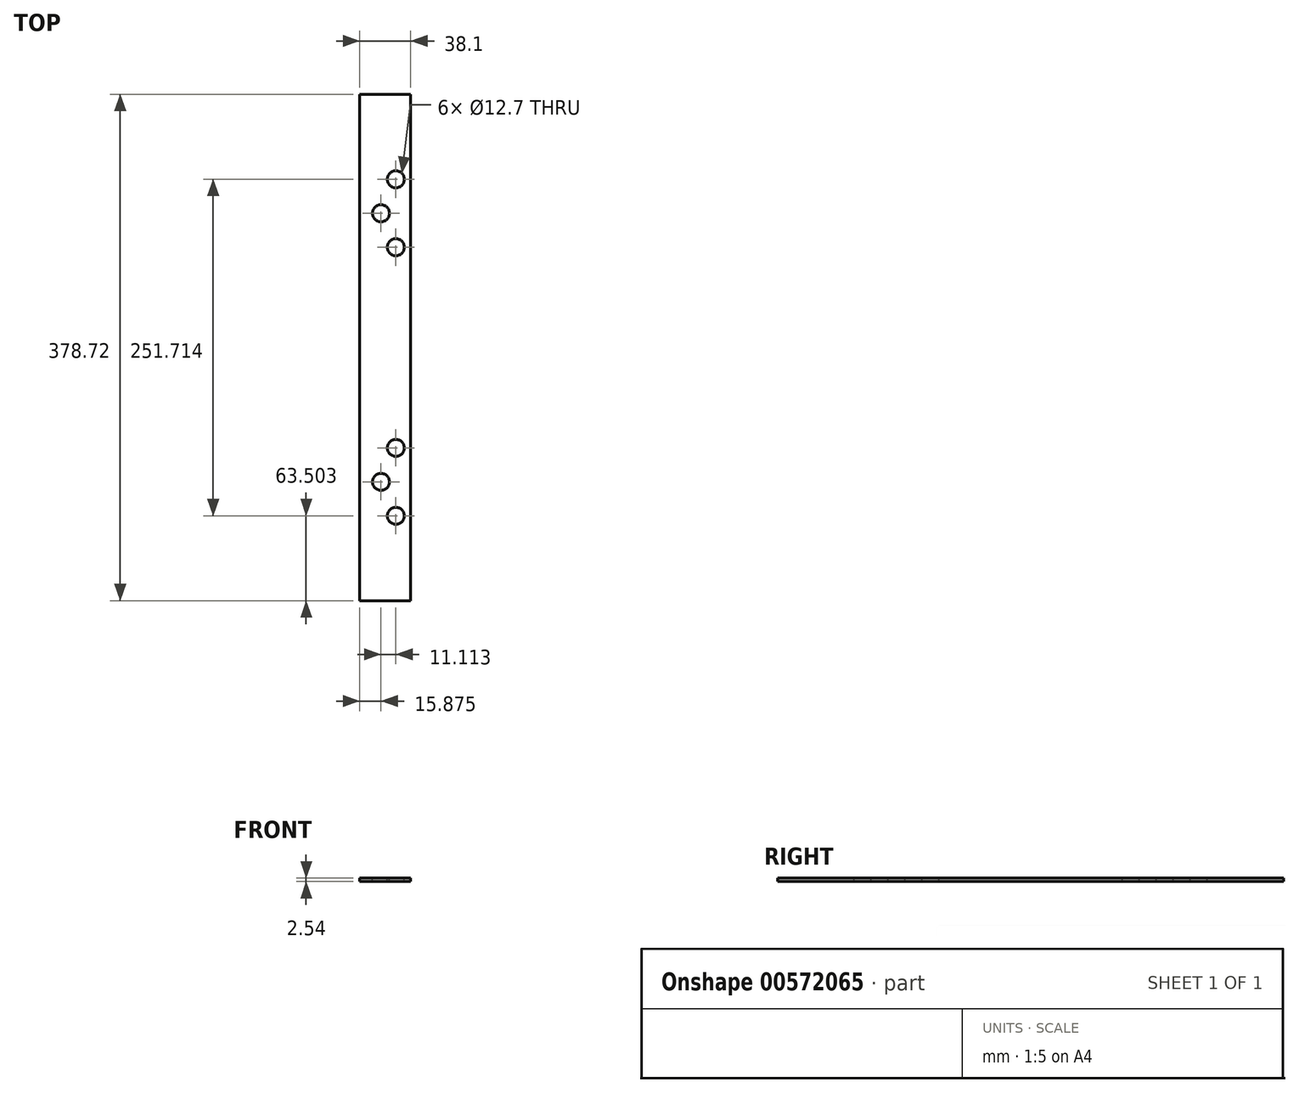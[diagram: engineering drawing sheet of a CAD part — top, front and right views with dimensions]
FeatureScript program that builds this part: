
annotation { "Feature Type Name" : "Feature", "Feature Type Description" : "" }
export const myFeature = defineFeature(function(context is Context, id is Id, definition is map)
    precondition{}
    {
        {
            var Q0;
            Q0=qCreatedBy(makeId("Top.planeOp"),FACE);
            var sketch = newSketch(context, id + "F0", { "sketchPlane" : qUnion([Q0])});
            skLineSegment(sketch, "E0.bottom", {"start": v(19.05, 189.36) * mm, "end": v(-19.05, 189.36) * mm});
            skLineSegment(sketch, "E0.top", {"start": v(19.05, -189.36) * mm, "end": v(-19.05, -189.36) * mm});
            skLineSegment(sketch, "E0.left", {"start": v(19.05, 189.36) * mm, "end": v(19.05, -189.36) * mm});
            skLineSegment(sketch, "E0.right", {"start": v(-19.05, 189.36) * mm, "end": v(-19.05, -189.36) * mm});
            skPoint(sketch, "E0.middle", {"position": v(0, 0) * mm});
            skSolve(sketch);
        }
        {
            var Q0;
            Q0=makeQuery(id+"F0.imprint","IMPRINT",FACE,{"disambiguationData":[TD([[makeQuery(id+"F0.imprint","IMPRINT",EDGE,{"derivedFrom":sQuery(id+"F0.wireOp",EDGE,"E0.bottom")}),1.0]])]});
            extrude(context, id + "F1", {"entities" : qUnion([Q0]), "depth" : 2.54 * mm, "offsetDistance" : 25.4 * mm});
        }
        {
            var Q0;
            Q0=makeQuery(id+"F1.opExtrude","CAP_FACE",FACE,{"disambiguationData":[OSD([sQuery(id+"F0.wireOp",EDGE,"E0.bottom"),sQuery(id+"F0.wireOp",EDGE,"E0.top"),sQuery(id+"F0.wireOp",EDGE,"E0.left"),sQuery(id+"F0.wireOp",EDGE,"E0.right")])],"isStart":false});
            var sketch = newSketch(context, id + "F2", { "sketchPlane" : qUnion([Q0])});
            skPoint(sketch, "E1", {"position": v(7.94, 125.86) * mm});
            skSolve(sketch);
        }
        {
            var Q0;
            Q0=makeQuery(id+"F2.imprint","IMPRINT",FACE,{"disambiguationData":[TD([[makeQuery(id+"F2.imprint","IMPRINT",EDGE,{"derivedFrom":makeQuery(id+"F1.opExtrude","CAP_EDGE",EDGE,{"disambiguationData":[OSD([sQuery(id+"F0.wireOp",EDGE,"E0.bottom")])],"isStart":false})}),1.0]])]});
            var sketch = newSketch(context, id + "F3", { "sketchPlane" : qUnion([Q0])});
            skPoint(sketch, "E2", {"position": v(7.94, 75.06) * mm});
            skSolve(sketch);
        }
        {
            var Q0;
            Q0=makeQuery(id+"F2.imprint","IMPRINT",FACE,{"disambiguationData":[TD([[makeQuery(id+"F2.imprint","IMPRINT",EDGE,{"derivedFrom":makeQuery(id+"F1.opExtrude","CAP_EDGE",EDGE,{"disambiguationData":[OSD([sQuery(id+"F0.wireOp",EDGE,"E0.bottom")])],"isStart":false})}),1.0]])]});
            var sketch = newSketch(context, id + "F4", { "sketchPlane" : qUnion([Q0])});
            skPoint(sketch, "E3", {"position": v(-3.17, 100.46) * mm});
            skSolve(sketch);
        }
        {
            var Q0;
            Q0=sQuery(id+"F4.wireOp",VERTEX,"E3");
            var Q1;
            Q1=sQuery(id+"F3.wireOp",VERTEX,"E2");
            var Q2;
            Q2=sQuery(id+"F2.wireOp",VERTEX,"E1");
            var Q3;
            Q3=makeQuery(id+"F1.opExtrude","SWEPT_BODY",BODY,{"disambiguationData":[OSD([sQuery(id+"F0.wireOp",EDGE,"E0.bottom"),sQuery(id+"F0.wireOp",EDGE,"E0.top"),sQuery(id+"F0.wireOp",EDGE,"E0.left"),sQuery(id+"F0.wireOp",EDGE,"E0.right")])]});
            hole(context, id + "F5", {"style" : HoleStyle.SIMPLE, "endStyle" : HoleEndStyle.THROUGH, "holeDiameter" : 12.7 * mm, "majorDiameter" : 6.35 * mm, "isTappedThrough" : true, "tappedDepth" : 12.7 * mm, "tapClearance" : 3, "locations" : qUnion([Q0, Q1, Q2]), "scope" : qUnion([Q3])});
        }
        {
            var Q0;
            Q0=makeQuery(id+"F1.opExtrude","CAP_FACE",FACE,{"disambiguationData":[OSD([sQuery(id+"F0.wireOp",EDGE,"E0.bottom"),sQuery(id+"F0.wireOp",EDGE,"E0.top"),sQuery(id+"F0.wireOp",EDGE,"E0.left"),sQuery(id+"F0.wireOp",EDGE,"E0.right")])],"isStart":false});
            var sketch = newSketch(context, id + "F6", { "sketchPlane" : qUnion([Q0])});
            skPoint(sketch, "E4", {"position": v(7.94, -125.86) * mm});
            skSolve(sketch);
        }
        {
            var Q0;
            Q0=makeQuery(id+"F6.imprint","IMPRINT",FACE,{"disambiguationData":[TD([[makeQuery(id+"F6.imprint","IMPRINT",EDGE,{"derivedFrom":makeQuery(id+"F1.opExtrude","CAP_EDGE",EDGE,{"disambiguationData":[OSD([sQuery(id+"F0.wireOp",EDGE,"E0.bottom")])],"isStart":false})}),1.0]])]});
            var sketch = newSketch(context, id + "F7", { "sketchPlane" : qUnion([Q0])});
            skPoint(sketch, "E5", {"position": v(7.94, -75.06) * mm});
            skSolve(sketch);
        }
        {
            var Q0;
            Q0=makeQuery(id+"F6.imprint","IMPRINT",FACE,{"disambiguationData":[TD([[makeQuery(id+"F6.imprint","IMPRINT",EDGE,{"derivedFrom":makeQuery(id+"F1.opExtrude","CAP_EDGE",EDGE,{"disambiguationData":[OSD([sQuery(id+"F0.wireOp",EDGE,"E0.bottom")])],"isStart":false})}),1.0]])]});
            var sketch = newSketch(context, id + "F8", { "sketchPlane" : qUnion([Q0])});
            skPoint(sketch, "E6", {"position": v(-3.18, -100.46) * mm});
            skSolve(sketch);
        }
        {
            var Q0;
            Q0=sQuery(id+"F6.wireOp",VERTEX,"E4");
            var Q1;
            Q1=sQuery(id+"F8.wireOp",VERTEX,"E6");
            var Q2;
            Q2=sQuery(id+"F7.wireOp",VERTEX,"E5");
            var Q3;
            Q3=makeQuery(id+"F1.opExtrude","SWEPT_BODY",BODY,{"disambiguationData":[OSD([sQuery(id+"F0.wireOp",EDGE,"E0.bottom"),sQuery(id+"F0.wireOp",EDGE,"E0.top"),sQuery(id+"F0.wireOp",EDGE,"E0.left"),sQuery(id+"F0.wireOp",EDGE,"E0.right")])]});
            hole(context, id + "F9", {"style" : HoleStyle.SIMPLE, "endStyle" : HoleEndStyle.THROUGH, "holeDiameter" : 12.7 * mm, "majorDiameter" : 6.35 * mm, "isTappedThrough" : true, "tappedDepth" : 12.7 * mm, "tapClearance" : 3, "locations" : qUnion([Q0, Q1, Q2]), "scope" : qUnion([Q3])});
        }
    });
